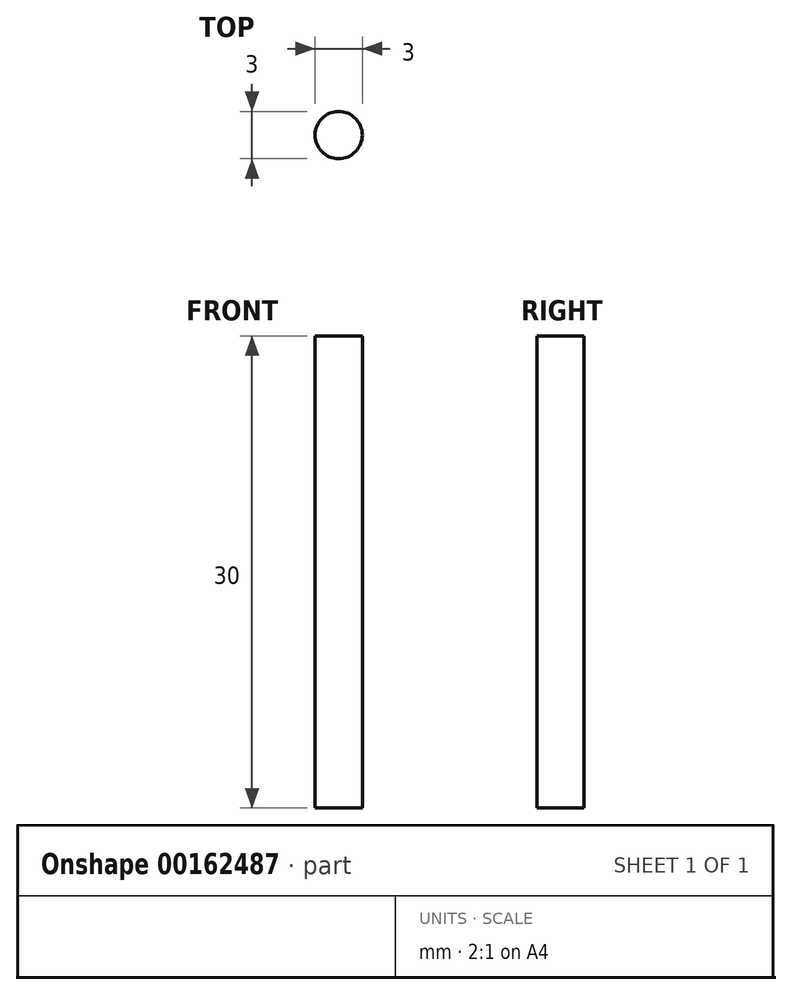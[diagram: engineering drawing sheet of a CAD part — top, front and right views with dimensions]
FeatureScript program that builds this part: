
annotation { "Feature Type Name" : "Feature", "Feature Type Description" : "" }
export const myFeature = defineFeature(function(context is Context, id is Id, definition is map)
    precondition{}
    {
        {
            var Q0;
            Q0=qCreatedBy(makeId("Top.planeOp"),FACE);
            var sketch = newSketch(context, id + "F0", { "sketchPlane" : qUnion([Q0])});
            skCircle(sketch, "E0", {"center": v(0, 0) * mm, "radius": 1.5 * mm});
            skSolve(sketch);
        }
        {
            var Q0;
            Q0=qSketchRegion(id+"F0",true);
            extrude(context, id + "F1", {"entities" : qUnion([Q0]), "depth" : 30 * mm});
        }
    });
